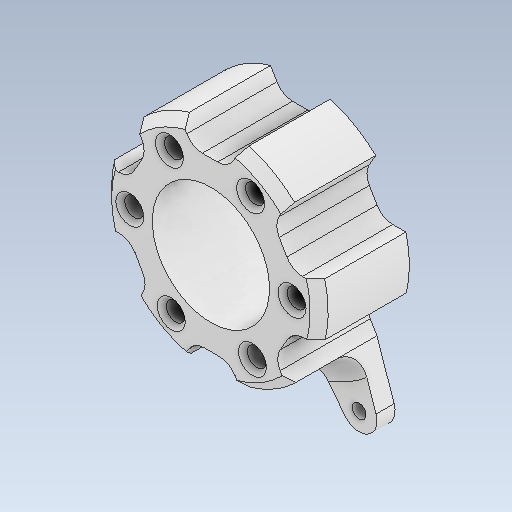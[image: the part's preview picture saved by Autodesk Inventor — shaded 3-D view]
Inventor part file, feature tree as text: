
AUTODESK INVENTOR PART (.ipt)
format: ipt  version: 2020 (Build 240168000, 168)  size: 310,784 bytes
history: native  units: mm
features: reference x9, other x4, extrude x3, sketch x3, chamfer x2, projected_geometry x2, pattern_circular x1, fillet x1
ambient origin geometry x8: Origin, YZ Plane, XZ Plane, XY Plane, X Axis, Y Axis, Z Axis, Center Point
bodies: Solid1 (feature_tree)
feature tree (25):
  extrude  "Extrusion1"  Depth=48.0mm
  extrude  "Extrusion2"  Depth=60.0mm TaperAngle=360.0deg
  pattern_circular  "Circular Pattern1"  Count=2  [1 undecoded]
  chamfer  "Chamfer1"  Distance=20.0mm
  extrude  "Extrusion3"  Depth=1.0mm TaperAngle=45.0deg
  fillet  "Fillet1"  Radius=8.0mm
  chamfer  "Chamfer2"  Distance=4.0mm
  sketch  "Sketch1"  dims[d0=26.0mm d1=48.0mm]
  reference  "Reference1"
  reference  "Reference2"
  reference  "Reference3"
  sketch  "Sketch2"  dims[d2=4.2mm d3=60.0mm d5=360.0deg d7=20.0mm d8=0.0mm d9=20.0mm d10=0.0mm]
  projected_geometry  "Projected Loop1"
  reference  "Reference4"
  reference  "Reference5"
  reference  "Reference6"
  reference  "Reference7"
  reference  "Reference8"
  sketch  "Sketch3"  dims[d11=60.0mm d12=360.0deg d14=1.0mm d15=2.0mm d16=45.0deg d17=8.0mm d18=4.0mm d19=0.0mm d20=5.0mm d21=2.0mm d22=2.0mm d23=45.0deg]
  reference  "Reference9"
  projected_geometry  "Projected Loop2"
  parser-record x1  (decoder bookkeeping rows leaked as tree rows — omitted from the tree; the rows remain in map.json)
  other  "reducer_3.iam"
  other  "joint_connector_1:1"
  other  "motor_h_3_m:1"
note: 1 required parameter value undecoded (feature->parameter linkage not recoverable at this tier; creation-order binding heuristic only, values carry confidence <= 0.55)
note: 1 file-system path scrubbed to <path> (originals preserved in map.json)
